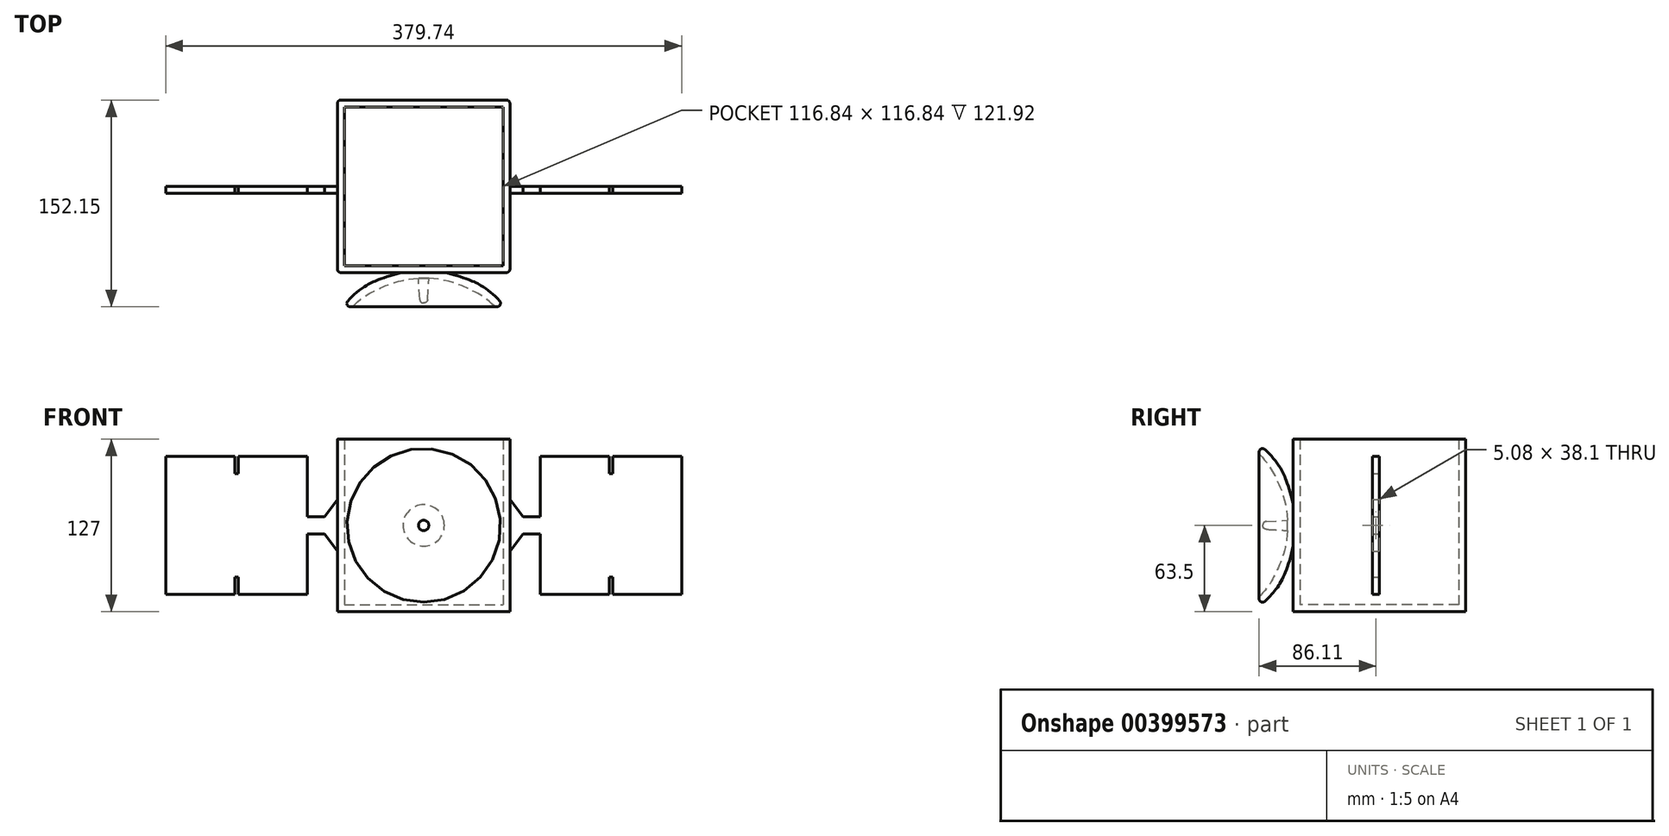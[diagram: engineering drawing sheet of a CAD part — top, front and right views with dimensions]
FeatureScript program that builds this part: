
annotation { "Feature Type Name" : "Feature", "Feature Type Description" : "" }
export const myFeature = defineFeature(function(context is Context, id is Id, definition is map)
    precondition{}
    {
        {
            var Q0;
            Q0=qCreatedBy(makeId("Top.planeOp"),FACE);
            var sketch = newSketch(context, id + "F0", { "sketchPlane" : qUnion([Q0])});
            skLineSegment(sketch, "E0.bottom", {"start": v(-63.5, 63.5) * mm, "end": v(63.5, 63.5) * mm});
            skLineSegment(sketch, "E0.top", {"start": v(-63.5, -63.5) * mm, "end": v(63.5, -63.5) * mm});
            skLineSegment(sketch, "E0.left", {"start": v(-63.5, 63.5) * mm, "end": v(-63.5, -63.5) * mm});
            skLineSegment(sketch, "E0.right", {"start": v(63.5, 63.5) * mm, "end": v(63.5, -63.5) * mm});
            skSolve(sketch);
        }
        {
            var Q0;
            Q0=makeQuery(id+"F0.imprint","IMPRINT",FACE,{"disambiguationData":[TD([[makeQuery(id+"F0.imprint","IMPRINT",EDGE,{"derivedFrom":sQuery(id+"F0.wireOp",EDGE,"E0.bottom")}),-1.0]])]});
            extrude(context, id + "F1", {"entities" : qUnion([Q0]), "depth" : 127 * mm});
        }
        {
            var Q0;
            Q0=makeQuery(id+"F1.opExtrude","CAP_FACE",FACE,{"disambiguationData":[OSD([sQuery(id+"F0.wireOp",EDGE,"E0.bottom"),sQuery(id+"F0.wireOp",EDGE,"E0.top"),sQuery(id+"F0.wireOp",EDGE,"E0.left"),sQuery(id+"F0.wireOp",EDGE,"E0.right")])],"isStart":false});
            shell(context, id + "F2", {"entities" : qUnion([Q0]), "thickness" : 5.08 * mm});
        }
        {
            var Q0;
            Q0=qCreatedBy(makeId("Front.planeOp"),FACE);
            cPlane(context, id + "F3", {"entities" : qUnion([Q0]), "cplaneType" : CPlaneType.OFFSET, "offset" : 63.5 * mm, "width" : 152.4 * mm, "height" : 152.4 * mm});
        }
        {
            var Q0;
            Q0=qCreatedBy(id+"F3.planeOp",FACE);
            cPlane(context, id + "F4", {"entities" : qUnion([Q0]), "cplaneType" : CPlaneType.OFFSET, "offset" : 25.4 * mm, "width" : 152.4 * mm, "height" : 152.4 * mm});
        }
        {
            var Q0;
            Q0=qCreatedBy(id+"F4.planeOp",FACE);
            var sketch = newSketch(context, id + "F5", { "sketchPlane" : qUnion([Q0])});
            skCircle(sketch, "E1", {"center": v(0, 63.5) * mm, "radius": 60.33 * mm});
            skSolve(sketch);
        }
        {
            var Q0;
            Q0=makeQuery(id+"F1.opExtrude","SWEPT_EDGE",EDGE,{"disambiguationData":[OSD([sQuery(id+"F0.wireOp",EDGE,"E0.top"),sQuery(id+"F0.wireOp",EDGE,"E0.left")])]});
            var Q1;
            Q1=makeQuery(id+"F1.opExtrude","SWEPT_EDGE",EDGE,{"disambiguationData":[OSD([sQuery(id+"F0.wireOp",EDGE,"E0.top"),sQuery(id+"F0.wireOp",EDGE,"E0.right")])]});
            var Q2;
            Q2=makeQuery(id+"F1.opExtrude","SWEPT_EDGE",EDGE,{"disambiguationData":[OSD([sQuery(id+"F0.wireOp",EDGE,"E0.bottom"),sQuery(id+"F0.wireOp",EDGE,"E0.right")])]});
            var Q3;
            Q3=makeQuery(id+"F1.opExtrude","SWEPT_EDGE",EDGE,{"disambiguationData":[OSD([sQuery(id+"F0.wireOp",EDGE,"E0.bottom"),sQuery(id+"F0.wireOp",EDGE,"E0.left")])]});
            fillet(context, id + "F6", {"entities" : qUnion([Q0, Q1, Q2, Q3]), "radius" : 2.54 * mm, "tangentPropagation" : true, "allowEdgeOverflow" : false});
        }
        {
            var Q0;
            Q0=qCreatedBy(makeId("Top.planeOp"),FACE);
            cPlane(context, id + "F7", {"entities" : qUnion([Q0]), "cplaneType" : CPlaneType.OFFSET, "offset" : 63.5 * mm, "width" : 152.4 * mm, "height" : 152.4 * mm});
        }
        {
            var Q0;
            Q0=qCreatedBy(id+"F7.planeOp",FACE);
            var sketch = newSketch(context, id + "F8", { "sketchPlane" : qUnion([Q0])});
            skFitSpline(sketch, "E2", {"points": [v(0, -67.62) * mm, v(-33.5, -75.72) * mm, v(-52.48, -88.6) * mm], "startDerivative": vector(-93.15, -1.6) * mm, "endDerivative": vector(-49.65, -50.04) * mm});
            skFitSpline(sketch, "E3", {"points": [v(-15.23, -63.5) * mm, v(-44.84, -74.72) * mm, v(-59.78, -88.82) * mm], "startDerivative": vector(-79.41, -18.33) * mm, "endDerivative": vector(-32.57, -39.1) * mm});
            skLineSegment(sketch, "E4", {"start": v(-15.23, -63.5) * mm, "end": v(0, -63.5) * mm});
            skLineSegment(sketch, "E5", {"start": v(-52.48, -88.6) * mm, "end": v(-59.78, -88.82) * mm});
            skLineSegment(sketch, "E6", {"start": v(0, -63.5) * mm, "end": v(0, -85.84) * mm});
            skLineSegment(sketch, "E7", {"start": v(0, -85.84) * mm, "end": v(-2.75, -85.84) * mm});
            skLineSegment(sketch, "E8", {"start": v(-2.75, -85.84) * mm, "end": v(-3.81, -67.76) * mm});
            skSolve(sketch);
        }
        {
            var Q0;
            Q0=qCreatedBy(makeId("Right.planeOp"),FACE);
            var sketch = newSketch(context, id + "F9", { "sketchPlane" : qUnion([Q0])});
            skLineSegment(sketch, "E9", {"start": v(-67.62, 63.5) * mm, "end": v(-88.6, 63.5) * mm});
            skSolve(sketch);
        }
        {
            var Q0;
            Q0 = qSketchRegion(id + "F8", true);
            var Q1;
            Q1=sQuery(id+"F9.wireOp",EDGE,"E9");
            revolve(context, id + "F10", {"entities" : qUnion([Q0]), "axis" : qUnion([Q1]), "revolveType" : RevolveType.FULL, "oppositeDirection" : true});
        }
        {
            var Q0;
            Q0=makeQuery(id+"F10.opRevolve","SWEPT_EDGE",EDGE,{"disambiguationData":[OSD([sQuery(id+"F8.wireOp",EDGE,"E3"),sQuery(id+"F8.wireOp",EDGE,"E5")])]});
            var Q1;
            Q1=makeQuery(id+"F10.opRevolve","SWEPT_EDGE",EDGE,{"disambiguationData":[OSD([sQuery(id+"F8.wireOp",EDGE,"E2"),sQuery(id+"F8.wireOp",EDGE,"E5")])]});
            fillet(context, id + "F11", {"entities" : qUnion([Q0, Q1]), "radius" : 2.54 * mm, "tangentPropagation" : true, "allowEdgeOverflow" : false});
        }
        {
            var Q0;
            Q0=makeQuery(id+"F10.opRevolve","SWEPT_EDGE",EDGE,{"disambiguationData":[OSD([sQuery(id+"F8.wireOp",EDGE,"E7"),sQuery(id+"F8.wireOp",EDGE,"E8")])]});
            fillet(context, id + "F12", {"entities" : qUnion([Q0]), "radius" : 2.54 * mm, "tangentPropagation" : true, "allowEdgeOverflow" : false});
        }
        {
            var Q0;
            Q0=qCreatedBy(makeId("Front.planeOp"),FACE);
            var sketch = newSketch(context, id + "F13", { "sketchPlane" : qUnion([Q0])});
            skLineSegment(sketch, "E10.bottom", {"start": v(-136.53, 114.3) * mm, "end": v(-85.73, 114.3) * mm});
            skLineSegment(sketch, "E10.top", {"start": v(-136.53, 12.7) * mm, "end": v(-85.73, 12.7) * mm});
            skLineSegment(sketch, "E10.left", {"start": v(-136.53, 114.3) * mm, "end": v(-136.53, 12.7) * mm});
            skLineSegment(sketch, "E10.right", {"start": v(-85.73, 114.3) * mm, "end": v(-85.73, 12.7) * mm});
            skLineSegment(sketch, "E11.bottom", {"start": v(-189.87, 114.3) * mm, "end": v(-139.07, 114.3) * mm});
            skLineSegment(sketch, "E11.top", {"start": v(-189.87, 12.7) * mm, "end": v(-139.07, 12.7) * mm});
            skLineSegment(sketch, "E11.left", {"start": v(-189.87, 114.3) * mm, "end": v(-189.87, 12.7) * mm});
            skLineSegment(sketch, "E11.right", {"start": v(-139.07, 114.3) * mm, "end": v(-139.07, 12.7) * mm});
            skLineSegment(sketch, "E12", {"start": v(-139.07, 101.6) * mm, "end": v(-136.53, 101.6) * mm});
            skLineSegment(sketch, "E13", {"start": v(-139.07, 25.4) * mm, "end": v(-136.53, 25.4) * mm});
            skLineSegment(sketch, "E14", {"start": v(-85.73, 69.85) * mm, "end": v(-73.03, 69.85) * mm});
            skLineSegment(sketch, "E15", {"start": v(-73.03, 69.85) * mm, "end": v(-63.5, 82.55) * mm});
            skLineSegment(sketch, "E16", {"start": v(-63.5, 82.55) * mm, "end": v(-63.5, 44.45) * mm});
            skLineSegment(sketch, "E17", {"start": v(-63.5, 44.45) * mm, "end": v(-73.02, 57.15) * mm});
            skLineSegment(sketch, "E18", {"start": v(-73.03, 57.15) * mm, "end": v(-85.73, 57.15) * mm});
            skLineSegment(sketch, "E19.MirrorCS", {"start": v(85.73, 69.85) * mm, "end": v(73.03, 69.85) * mm});
            skLineSegment(sketch, "E20.MirrorCS", {"start": v(73.03, 57.15) * mm, "end": v(85.73, 57.15) * mm});
            skLineSegment(sketch, "E21.MirrorCS", {"start": v(136.53, 114.3) * mm, "end": v(85.73, 114.3) * mm});
            skLineSegment(sketch, "E22.MirrorCS", {"start": v(139.07, 101.6) * mm, "end": v(136.53, 101.6) * mm});
            skLineSegment(sketch, "E23.MirrorCS", {"start": v(139.07, 25.4) * mm, "end": v(136.53, 25.4) * mm});
            skLineSegment(sketch, "E24.MirrorCS", {"start": v(73.03, 69.85) * mm, "end": v(63.5, 82.55) * mm});
            skLineSegment(sketch, "E25.MirrorCS", {"start": v(85.73, 114.3) * mm, "end": v(85.73, 12.7) * mm});
            skLineSegment(sketch, "E26.MirrorCS", {"start": v(136.53, 114.3) * mm, "end": v(136.53, 12.7) * mm});
            skLineSegment(sketch, "E27.MirrorCS", {"start": v(189.87, 12.7) * mm, "end": v(139.07, 12.7) * mm});
            skLineSegment(sketch, "E28.MirrorCS", {"start": v(189.87, 114.3) * mm, "end": v(189.87, 12.7) * mm});
            skLineSegment(sketch, "E29.MirrorCS", {"start": v(139.07, 114.3) * mm, "end": v(139.07, 12.7) * mm});
            skLineSegment(sketch, "E30.MirrorCS", {"start": v(63.5, 82.55) * mm, "end": v(63.5, 44.45) * mm});
            skLineSegment(sketch, "E31.MirrorCS", {"start": v(63.5, 44.45) * mm, "end": v(73.02, 57.15) * mm});
            skLineSegment(sketch, "E32.MirrorCS", {"start": v(136.53, 12.7) * mm, "end": v(85.73, 12.7) * mm});
            skLineSegment(sketch, "E33.MirrorCS", {"start": v(189.87, 114.3) * mm, "end": v(139.07, 114.3) * mm});
            skSolve(sketch);
        }
        {
            var Q0;
            Q0 = qSketchRegion(id + "F13", true);
            extrude(context, id + "F14", {"entities" : qUnion([Q0]), "operationType" : NewBodyOperationType.ADD, "depth" : 5.08 * mm});
        }
    });
